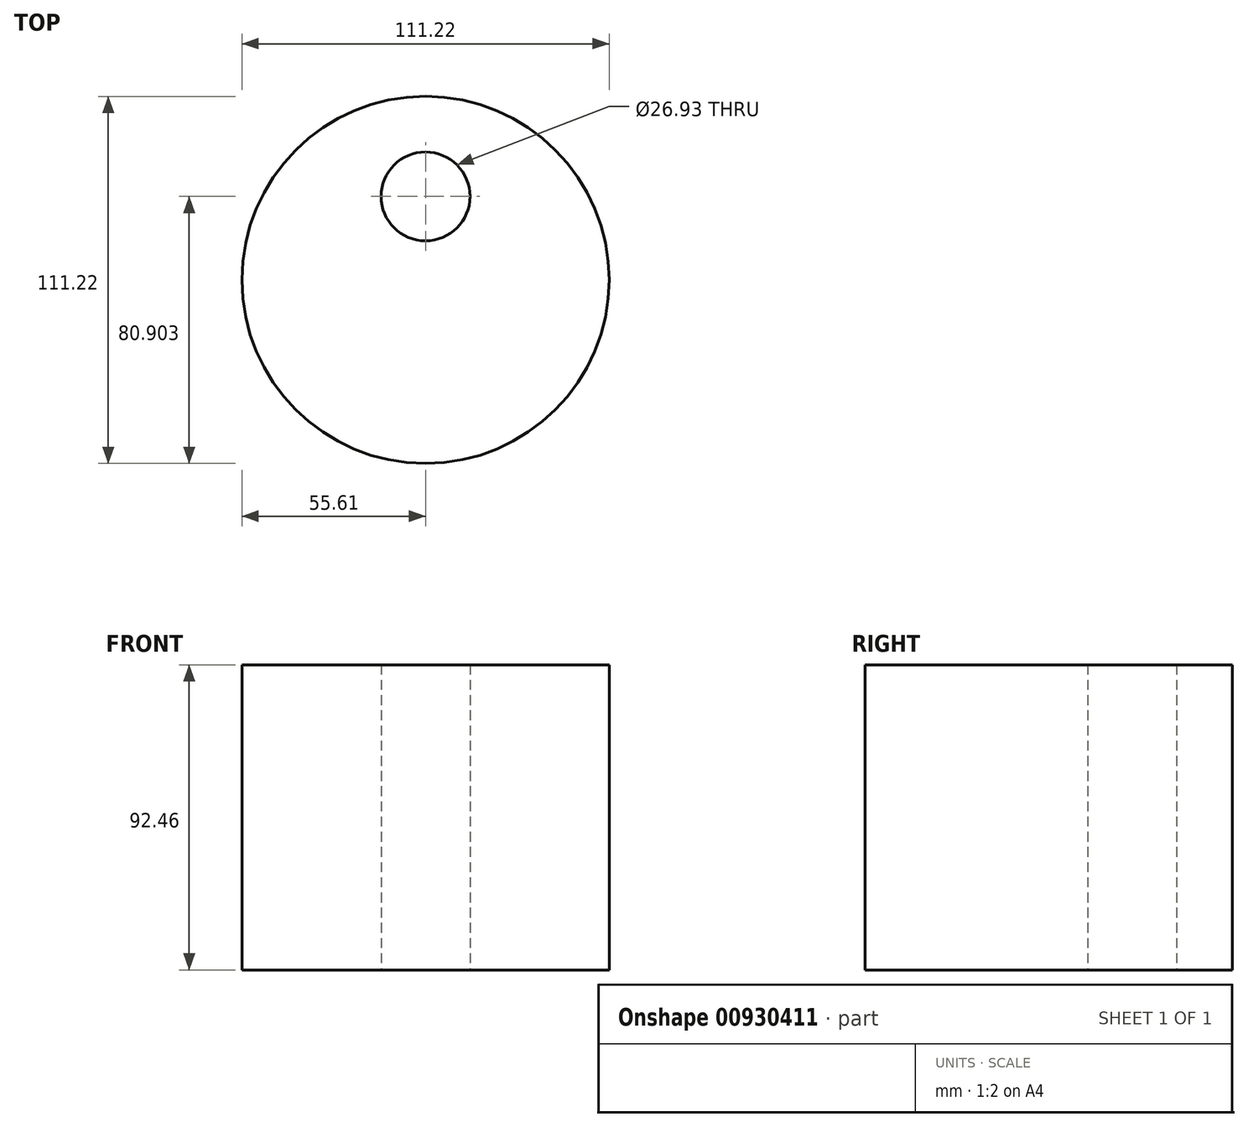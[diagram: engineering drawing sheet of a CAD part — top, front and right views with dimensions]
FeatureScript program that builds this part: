
annotation { "Feature Type Name" : "Feature", "Feature Type Description" : "" }
export const myFeature = defineFeature(function(context is Context, id is Id, definition is map)
    precondition{}
    {
        {
            var Q0;
            Q0=qCreatedBy(makeId("Top.planeOp"),FACE);
            var sketch = newSketch(context, id + "F0", { "sketchPlane" : qUnion([Q0])});
            skCircle(sketch, "E0", {"center": v(0, 0) * mm, "radius": 55.61 * mm});
            skCircle(sketch, "E1", {"center": v(0, 25.3) * mm, "radius": 13.47 * mm});
            skSolve(sketch);
        }
        {
            var Q0;
            Q0=makeQuery(id+"F0.imprint","IMPRINT",FACE,{"disambiguationData":[TD([[makeQuery(id+"F0.imprint","IMPRINT",EDGE,{"derivedFrom":sQuery(id+"F0.wireOp",EDGE,"E0")}),1.0]])]});
            extrude(context, id + "F1", {"entities" : qUnion([Q0]), "depth" : 92.46 * mm, "offsetDistance" : 25.4 * mm});
        }
    });
